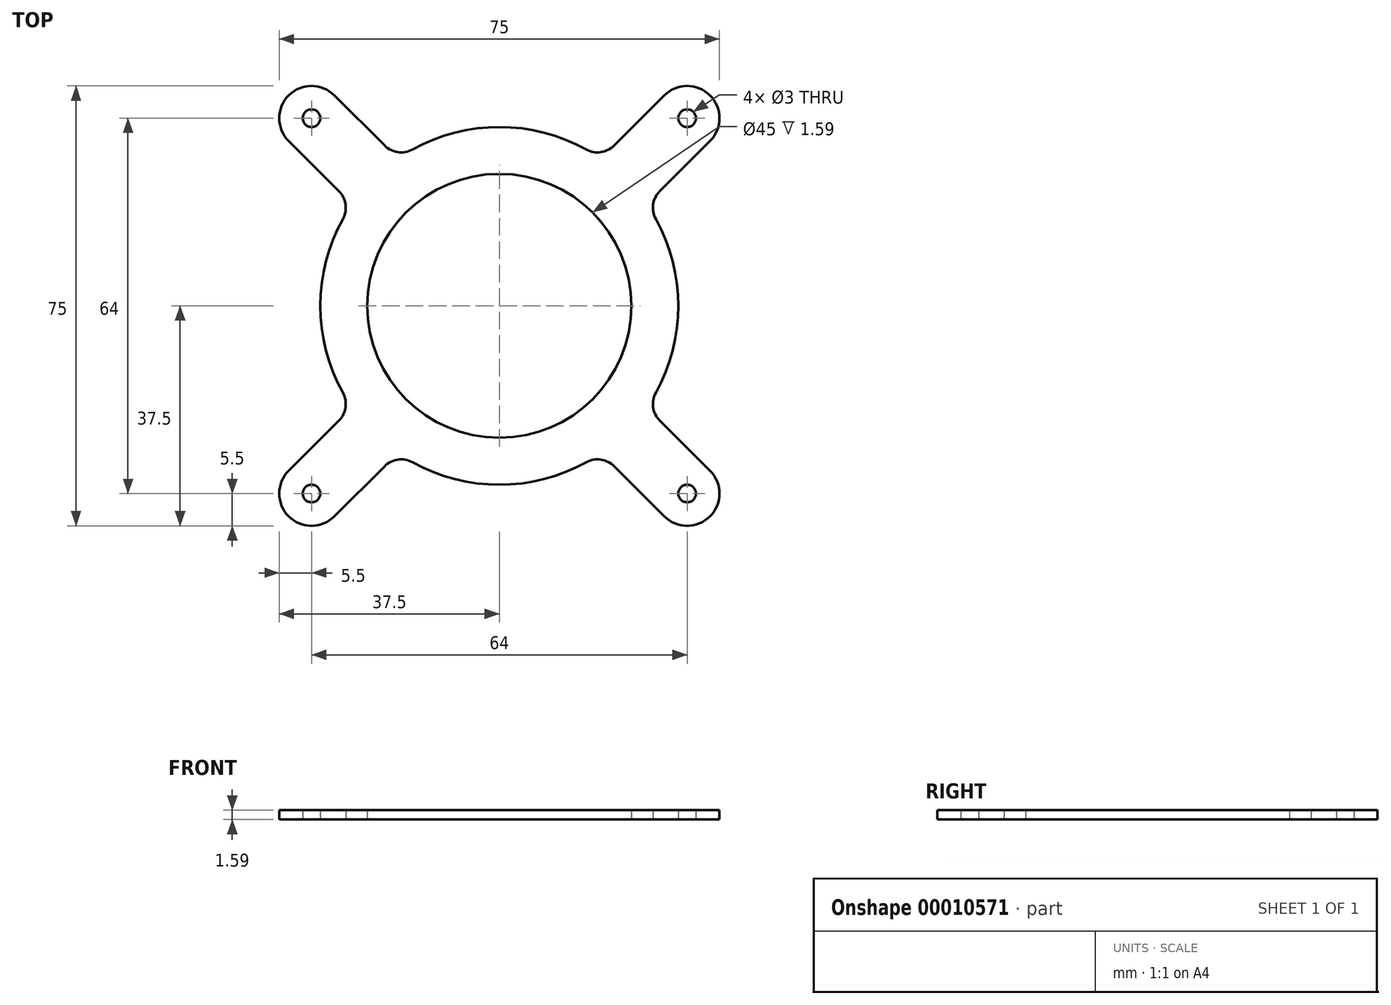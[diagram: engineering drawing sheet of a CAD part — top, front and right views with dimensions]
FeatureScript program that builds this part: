
annotation { "Feature Type Name" : "Feature", "Feature Type Description" : "" }
export const myFeature = defineFeature(function(context is Context, id is Id, definition is map)
    precondition{}
    {
        {
            var Q0;
            Q0=qCreatedBy(makeId("Top.planeOp"),FACE);
            var sketch = newSketch(context, id + "F0", { "sketchPlane" : qUnion([Q0])});
            skCircle(sketch, "E0", {"center": v(-32, -32) * mm, "radius": 1.5 * mm});
            skCircle(sketch, "E1", {"center": v(-32, 32) * mm, "radius": 1.5 * mm});
            skCircle(sketch, "E2", {"center": v(32, 32) * mm, "radius": 1.5 * mm});
            skCircle(sketch, "E3", {"center": v(32, -32) * mm, "radius": 1.5 * mm});
            skLineSegment(sketch, "E4", {"start": v(-32, 32) * mm, "end": v(-32, -32) * mm, "construction": true});
            skLineSegment(sketch, "E5", {"start": v(-32, -32) * mm, "end": v(32, -32) * mm, "construction": true});
            skLineSegment(sketch, "E6", {"start": v(-32, 32) * mm, "end": v(32, 32) * mm, "construction": true});
            skLineSegment(sketch, "E7", {"start": v(32, -32) * mm, "end": v(32, 32) * mm, "construction": true});
            skCircle(sketch, "E8", {"center": v(0, 0) * mm, "radius": 22.5 * mm});
            skCircle(sketch, "E9.0", {"center": v(0, 0) * mm, "radius": 30.5 * mm});
            skCircle(sketch, "E10.0", {"center": v(-32, 32) * mm, "radius": 5.5 * mm});
            skLineSegment(sketch, "E11", {"start": v(-35.89, 28.11) * mm, "end": v(-25.1, 17.32) * mm});
            skLineSegment(sketch, "E12", {"start": v(-28.11, 35.89) * mm, "end": v(-17.32, 25.1) * mm});
            skLineSegment(sketch, "E13", {"start": v(0, 0) * mm, "end": v(-32, 32) * mm, "construction": true});
            skCircle(sketch, "E14", {"center": v(32, 32) * mm, "radius": 5.5 * mm});
            skCircle(sketch, "E15", {"center": v(32, -32) * mm, "radius": 5.5 * mm});
            skCircle(sketch, "E16", {"center": v(-32, -32) * mm, "radius": 5.5 * mm});
            skLineSegment(sketch, "E17", {"start": v(0, 0) * mm, "end": v(32, 32) * mm, "construction": true});
            skLineSegment(sketch, "E18", {"start": v(0, 0) * mm, "end": v(32, -32) * mm, "construction": true});
            skLineSegment(sketch, "E19", {"start": v(0, 0) * mm, "end": v(-32, -32) * mm, "construction": true});
            skLineSegment(sketch, "E20", {"start": v(-35.89, -28.11) * mm, "end": v(-25.1, -17.32) * mm});
            skLineSegment(sketch, "E21", {"start": v(-28.11, -35.89) * mm, "end": v(-17.32, -25.1) * mm});
            skLineSegment(sketch, "E22", {"start": v(28.11, -35.89) * mm, "end": v(17.32, -25.1) * mm});
            skLineSegment(sketch, "E23", {"start": v(35.89, -28.11) * mm, "end": v(25.1, -17.32) * mm});
            skLineSegment(sketch, "E24", {"start": v(35.89, 28.11) * mm, "end": v(25.1, 17.32) * mm});
            skLineSegment(sketch, "E25", {"start": v(28.11, 35.89) * mm, "end": v(17.32, 25.1) * mm});
            skSolve(sketch);
        }
        {
            var Q0;
            Q0=makeQuery(id+"F0.imprint","IMPRINT",FACE,{"disambiguationData":[TD([[makeQuery(id+"F0.imprint","IMPRINT",EDGE,{"derivedFrom":sQuery(id+"F0.wireOp",EDGE,"E8")}),-1.0]])]});
            var Q1;
            {var subQ1=sQuery(id+"F0.wireOp",EDGE,"E20");Q1=makeQuery(id+"F0.imprint","IMPRINT",FACE,{"disambiguationData":[TD([[makeQuery(id+"F0.imprint","IMPRINT",EDGE,{"derivedFrom":subQ1}),-1.0]])]});}
            var Q2;
            {var subQ1=sQuery(id+"F0.wireOp",EDGE,"E22");Q2=makeQuery(id+"F0.imprint","IMPRINT",FACE,{"disambiguationData":[TD([[makeQuery(id+"F0.imprint","IMPRINT",EDGE,{"derivedFrom":subQ1}),-1.0]])]});}
            var Q3;
            {var subQ1=sQuery(id+"F0.wireOp",EDGE,"E24");Q3=makeQuery(id+"F0.imprint","IMPRINT",FACE,{"disambiguationData":[TD([[makeQuery(id+"F0.imprint","IMPRINT",EDGE,{"derivedFrom":subQ1}),-1.0]])]});}
            var Q4;
            Q4=makeQuery(id+"F0.imprint","IMPRINT",FACE,{"disambiguationData":[TD([[makeQuery(id+"F0.imprint","IMPRINT",EDGE,{"derivedFrom":sQuery(id+"F0.wireOp",EDGE,"E0")}),-1.0]])]});
            var Q5;
            Q5=makeQuery(id+"F0.imprint","IMPRINT",FACE,{"disambiguationData":[TD([[makeQuery(id+"F0.imprint","IMPRINT",EDGE,{"derivedFrom":sQuery(id+"F0.wireOp",EDGE,"E3")}),-1.0]])]});
            var Q6;
            Q6=makeQuery(id+"F0.imprint","IMPRINT",FACE,{"disambiguationData":[TD([[makeQuery(id+"F0.imprint","IMPRINT",EDGE,{"derivedFrom":sQuery(id+"F0.wireOp",EDGE,"E2")}),-1.0]])]});
            var Q7;
            Q7=makeQuery(id+"F0.imprint","IMPRINT",FACE,{"disambiguationData":[TD([[makeQuery(id+"F0.imprint","IMPRINT",EDGE,{"derivedFrom":sQuery(id+"F0.wireOp",EDGE,"E1")}),-1.0]])]});
            var Q8;
            {var subQ1=sQuery(id+"F0.wireOp",EDGE,"E11");Q8=makeQuery(id+"F0.imprint","IMPRINT",FACE,{"disambiguationData":[TD([[makeQuery(id+"F0.imprint","IMPRINT",EDGE,{"derivedFrom":subQ1}),1.0]])]});}
            extrude(context, id + "F1", {"entities" : qUnion([Q0, Q1, Q2, Q3, Q4, Q5, Q6, Q7, Q8]), "depth" : 1.59 * mm});
        }
        {
            var Q0;
            Q0=makeQuery(id+"F1.opExtrude","SWEPT_EDGE",EDGE,{"disambiguationData":[OSD([sQuery(id+"F0.wireOp",EDGE,"E9.0"),sQuery(id+"F0.wireOp",EDGE,"E21")])]});
            var Q1;
            Q1=makeQuery(id+"F1.opExtrude","SWEPT_EDGE",EDGE,{"disambiguationData":[OSD([sQuery(id+"F0.wireOp",EDGE,"E9.0"),sQuery(id+"F0.wireOp",EDGE,"E22")])]});
            var Q2;
            Q2=makeQuery(id+"F1.opExtrude","SWEPT_EDGE",EDGE,{"disambiguationData":[OSD([sQuery(id+"F0.wireOp",EDGE,"E9.0"),sQuery(id+"F0.wireOp",EDGE,"E23")])]});
            var Q3;
            Q3=makeQuery(id+"F1.opExtrude","SWEPT_EDGE",EDGE,{"disambiguationData":[OSD([sQuery(id+"F0.wireOp",EDGE,"E9.0"),sQuery(id+"F0.wireOp",EDGE,"E24")])]});
            var Q4;
            Q4=makeQuery(id+"F1.opExtrude","SWEPT_EDGE",EDGE,{"disambiguationData":[OSD([sQuery(id+"F0.wireOp",EDGE,"E9.0"),sQuery(id+"F0.wireOp",EDGE,"E25")])]});
            var Q5;
            Q5=makeQuery(id+"F1.opExtrude","SWEPT_EDGE",EDGE,{"disambiguationData":[OSD([sQuery(id+"F0.wireOp",EDGE,"E9.0"),sQuery(id+"F0.wireOp",EDGE,"E12")])]});
            var Q6;
            Q6=makeQuery(id+"F1.opExtrude","SWEPT_EDGE",EDGE,{"disambiguationData":[OSD([sQuery(id+"F0.wireOp",EDGE,"E9.0"),sQuery(id+"F0.wireOp",EDGE,"E11")])]});
            var Q7;
            Q7=makeQuery(id+"F1.opExtrude","SWEPT_EDGE",EDGE,{"disambiguationData":[OSD([sQuery(id+"F0.wireOp",EDGE,"E9.0"),sQuery(id+"F0.wireOp",EDGE,"E20")])]});
            fillet(context, id + "F2", {"entities" : qUnion([Q0, Q1, Q2, Q3, Q4, Q5, Q6, Q7]), "radius" : 4 * mm, "tangentPropagation" : true, "allowEdgeOverflow" : false});
        }
    });
